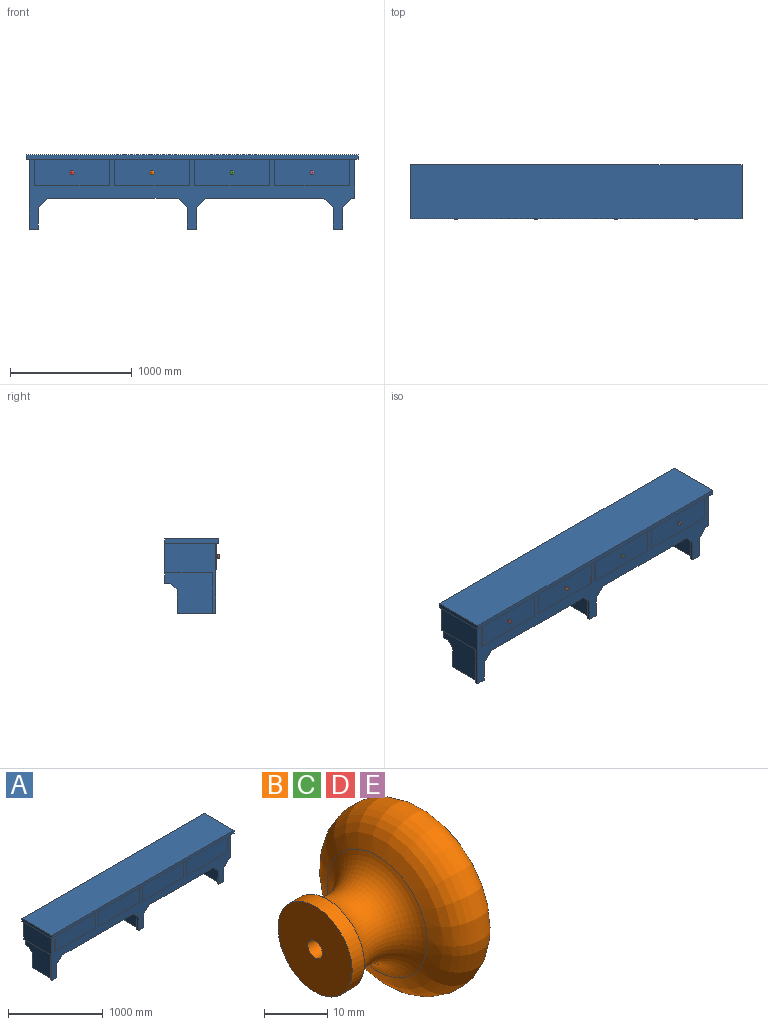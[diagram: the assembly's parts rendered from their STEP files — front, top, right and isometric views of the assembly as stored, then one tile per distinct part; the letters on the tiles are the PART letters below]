
ASSEMBLY  parts=5 mates=4
PART A: 64 faces, bbox 2724.2x444.5x609.6 mm
  f0: plane 2724.15x368.3mm, normal (0,1,0), area 755643.6mm2, adj f4,f5,f6,f10,f14,f16,f17,f18
  f1: plane 190.5x25.4mm, normal (0,1,0), area 4838.7mm2, adj f8,f15,f50,f60
  f2: plane 190.5x25.4mm, normal (0,1,0), area 4838.7mm2, adj f7,f12,f51,f55
  f3: plane 190.5x25.4mm, normal (0,1,0), area 4838.7mm2, adj f9,f13,f54,f58
  f4: plane 50.8x25.4mm, normal (0,0,-1), area 1290.3mm2, adj f0,f7,f51,f55
  f5: plane 50.8x25.4mm, normal (0,0,-1), area 1290.3mm2, adj f0,f8,f50,f60
  f6: plane 50.8x25.4mm, normal (0,0,-1), area 1290.3mm2, adj f0,f9,f54,f58
  f7: plane 50.8x50.8mm, normal (0,0.71,-0.71), area 1824.8mm2, adj f2,f4,f51,f55
  f8: plane 50.8x50.8mm, normal (0,0.71,-0.71), area 1824.8mm2, adj f1,f5,f50,f60
  f9: plane 50.8x50.8mm, normal (0,0.71,-0.71), area 1824.8mm2, adj f3,f6,f54,f58
  f10: plane 571.5x419.1mm, normal (-1,0,0), area 109515.9mm2, adj f0,f11,f15,f19,f61,f62
  f11: plane 2673.35x571.5mm, normal (0,-1,0), area 394918.6mm2, adj f10,f12,f13,f14,f15,f19,f20,f21
  f12: plane 317.5x76.2mm, normal (0,0,-1), area 9354.8mm2, adj f2,f11,f24,f30,f49,f51,f53,f55
  f13: plane 317.5x76.2mm, normal (0,0,-1), area 9354.8mm2, adj f3,f11,f21,f25,f53,f54,f57,f58
  f14: plane 419.1x317.5mm, normal (1,0,0), area 103064.3mm2, adj f0,f11,f19,f20,f57,f59
  f15: plane 317.5x76.2mm, normal (0,0,-1), area 9354.8mm2, adj f1,f10,f11,f29,f49,f50,f60,f61
  f16: plane 444.5x38.1mm, normal (-1,0,0), area 16935.5mm2, adj f0,f18,f19,f63
  f17: plane 444.5x38.1mm, normal (1,0,0), area 16935.5mm2, adj f0,f18,f19,f63
  f18: plane 2724.15x444.5mm, normal (0,0,1), area 1210884.7mm2, adj f0,f16,f17,f63
  f19: plane 2724.15x444.5mm, normal (0,0,-1), area 84290.2mm2, adj f0,f10,f11,f14,f16,f17,f33,f35
  f20: plane 25.4x25.4mm, normal (0,0,-1), area 645.2mm2, adj f11,f14,f22,f57
  f21: plane 177.8x25.4mm, normal (1,0,0), area 4516.1mm2, adj f11,f13,f22,f57
  f22: plane 76.2x76.2mm, normal (0.71,0,-0.71), area 2737.2mm2, adj f11,f20,f21,f57
  f23: plane 968.38x25.4mm, normal (0,0,-1), area 24596.7mm2, adj f11,f26,f27,f53
  f24: plane 177.8x25.4mm, normal (1,0,0), area 4516.1mm2, adj f11,f12,f27,f53
  f25: plane 177.8x25.4mm, normal (-1,0,0), area 4516.1mm2, adj f11,f13,f26,f53
  f26: plane 76.2x76.2mm, normal (-0.71,0,-0.71), area 2737.2mm2, adj f11,f23,f25,f53
  f27: plane 76.2x76.2mm, normal (0.71,0,-0.71), area 2737.2mm2, adj f11,f23,f24,f53
  f28: plane 1069.98x25.4mm, normal (0,0,-1), area 27177.4mm2, adj f11,f31,f32,f49
  f29: plane 177.8x25.4mm, normal (1,0,0), area 4516.1mm2, adj f11,f15,f32,f49
  f30: plane 177.8x25.4mm, normal (-1,0,0), area 4516.1mm2, adj f11,f12,f31,f49
  f31: plane 76.2x76.2mm, normal (-0.71,0,-0.71), area 2737.2mm2, adj f11,f28,f30,f49
  f32: plane 76.2x76.2mm, normal (0.71,0,-0.71), area 2737.2mm2, adj f11,f28,f29,f49
  f33: plane 215.9x2.54mm, normal (-1,0,0), area 548.4mm2, adj f11,f19,f34,f36
  f34: plane 609.6x2.54mm, normal (0,0,-1), area 1548.4mm2, adj f11,f33,f35,f36
  f35: plane 215.9x2.54mm, normal (1,0,0), area 548.4mm2, adj f11,f19,f34,f36
  f36: plane 609.6x215.9mm, normal (0,-1,0), area 131612.6mm2, adj f19,f33,f34,f35
  f37: plane 215.9x2.54mm, normal (-1,0,0), area 548.4mm2, adj f11,f19,f38,f40
  f38: plane 609.6x2.54mm, normal (0,0,-1), area 1548.4mm2, adj f11,f37,f39,f40
  f39: plane 215.9x2.54mm, normal (1,0,0), area 548.4mm2, adj f11,f19,f38,f40
  f40: plane 609.6x215.9mm, normal (0,-1,0), area 131612.6mm2, adj f19,f37,f38,f39
  f41: plane 215.9x2.54mm, normal (-1,0,0), area 548.4mm2, adj f11,f19,f42,f44
  f42: plane 609.6x2.54mm, normal (0,0,-1), area 1548.4mm2, adj f11,f41,f43,f44
  f43: plane 215.9x2.54mm, normal (1,0,0), area 548.4mm2, adj f11,f19,f42,f44
  f44: plane 609.6x215.9mm, normal (0,-1,0), area 131612.6mm2, adj f19,f41,f42,f43
  f45: plane 215.9x2.54mm, normal (-1,0,0), area 548.4mm2, adj f11,f19,f46,f48
  f46: plane 609.6x2.54mm, normal (0,0,-1), area 1548.4mm2, adj f11,f45,f47,f48
  f47: plane 215.9x2.54mm, normal (1,0,0), area 548.4mm2, adj f11,f19,f46,f48
  f48: plane 609.6x215.9mm, normal (0,-1,0), area 131612.6mm2, adj f19,f45,f46,f47
  f49: plane 1273.18x330.2mm, normal (0,1,0), area 115725.6mm2, adj f12,f15,f28,f29,f30,f31,f32,f50
  f50: plane 393.7x330.2mm, normal (1,0,0), area 106774mm2, adj f0,f1,f5,f8,f15,f49,f52
  f51: plane 393.7x330.2mm, normal (-1,0,0), area 106774mm2, adj f0,f2,f4,f7,f12,f49,f52
  f52: plane 1273.18x393.7mm, normal (0,0,-1), area 501249mm2, adj f0,f49,f50,f51
  f53: plane 1171.58x330.2mm, normal (0,1,0), area 107983.7mm2, adj f12,f13,f23,f24,f25,f26,f27,f54
  f54: plane 393.7x330.2mm, normal (-1,0,0), area 106774mm2, adj f0,f3,f6,f9,f13,f53,f56
  f55: plane 393.7x330.2mm, normal (1,0,0), area 106774mm2, adj f0,f2,f4,f7,f12,f53,f56
  f56: plane 1171.58x393.7mm, normal (0,0,-1), area 461249.1mm2, adj f0,f53,f54,f55
  f57: plane 330.2x127mm, normal (0,1,0), area 19032.2mm2, adj f13,f14,f20,f21,f22,f58,f59
  f58: plane 393.7x330.2mm, normal (1,0,0), area 106774mm2, adj f0,f3,f6,f9,f13,f57,f59
  f59: plane 393.7x127mm, normal (0,0,-1), area 49999.9mm2, adj f0,f14,f57,f58
  f60: plane 393.7x330.2mm, normal (-1,0,0), area 106774mm2, adj f0,f1,f5,f8,f15,f61,f62
  f61: plane 330.2x25.4mm, normal (0,1,0), area 8387.1mm2, adj f10,f15,f60,f62
  f62: plane 393.7x25.4mm, normal (0,0,-1), area 10000mm2, adj f0,f10,f60,f61
  f63: plane 2724.15x38.1mm, normal (0,-1,0), area 103790.1mm2, adj f16,f17,f18,f19
PART B: 6 faces, bbox 27x33.8x33.8 mm
  f0: revolved ~33.77x33.77mm, area 2051mm2, adj f5
  f1: cylinder r=8.33mm len=16.65mm, axis (-1,0,0), area 143.8mm2, adj f2,f5
  f2: plane 16.65x16.65mm, normal (-1,0,0), area 209.2mm2, adj f1,f3
  f3: cylinder r=1.65mm len=10mm, axis (-1,0,0), area 103.7mm2, adj f2,f4
  f4: plane 3.3x3.3mm, normal (-1,0,0), area 8.6mm2, adj f3
  f5: torus R=13.28mm, axis (-1,0,0), area 669.8mm2, adj f0,f1
PART C: same geometry as B
PART D: same geometry as B
PART E: same geometry as B
PLACE A at identity
PLACE B rot(axis=(0,0,-1),90deg) t=(-328.29,-460.36,-146.05)mm
PLACE C rot(axis=(0,0,-1),90deg) t=(328.3,-460.36,-146.05)mm
PLACE D rot(axis=(0,0,-1),90deg) t=(-984.88,-460.36,-146.05)mm
PLACE E rot(axis=(0,0,-1),90deg) t=(984.89,-460.36,-146.05)mm
MATE planar D.f1 <-> A.f36  axis (0,1,0) through (-984.88,-421.64,-146.05)mm
MATE planar E.f1 <-> A.f48  axis (0,1,0) through (984.89,-421.64,-146.05)mm
MATE planar B.f1 <-> A.f40  axis (0,1,0) through (-328.29,-421.64,-146.05)mm
MATE planar C.f1 <-> A.f44  axis (0,1,0) through (328.3,-421.64,-146.05)mm
